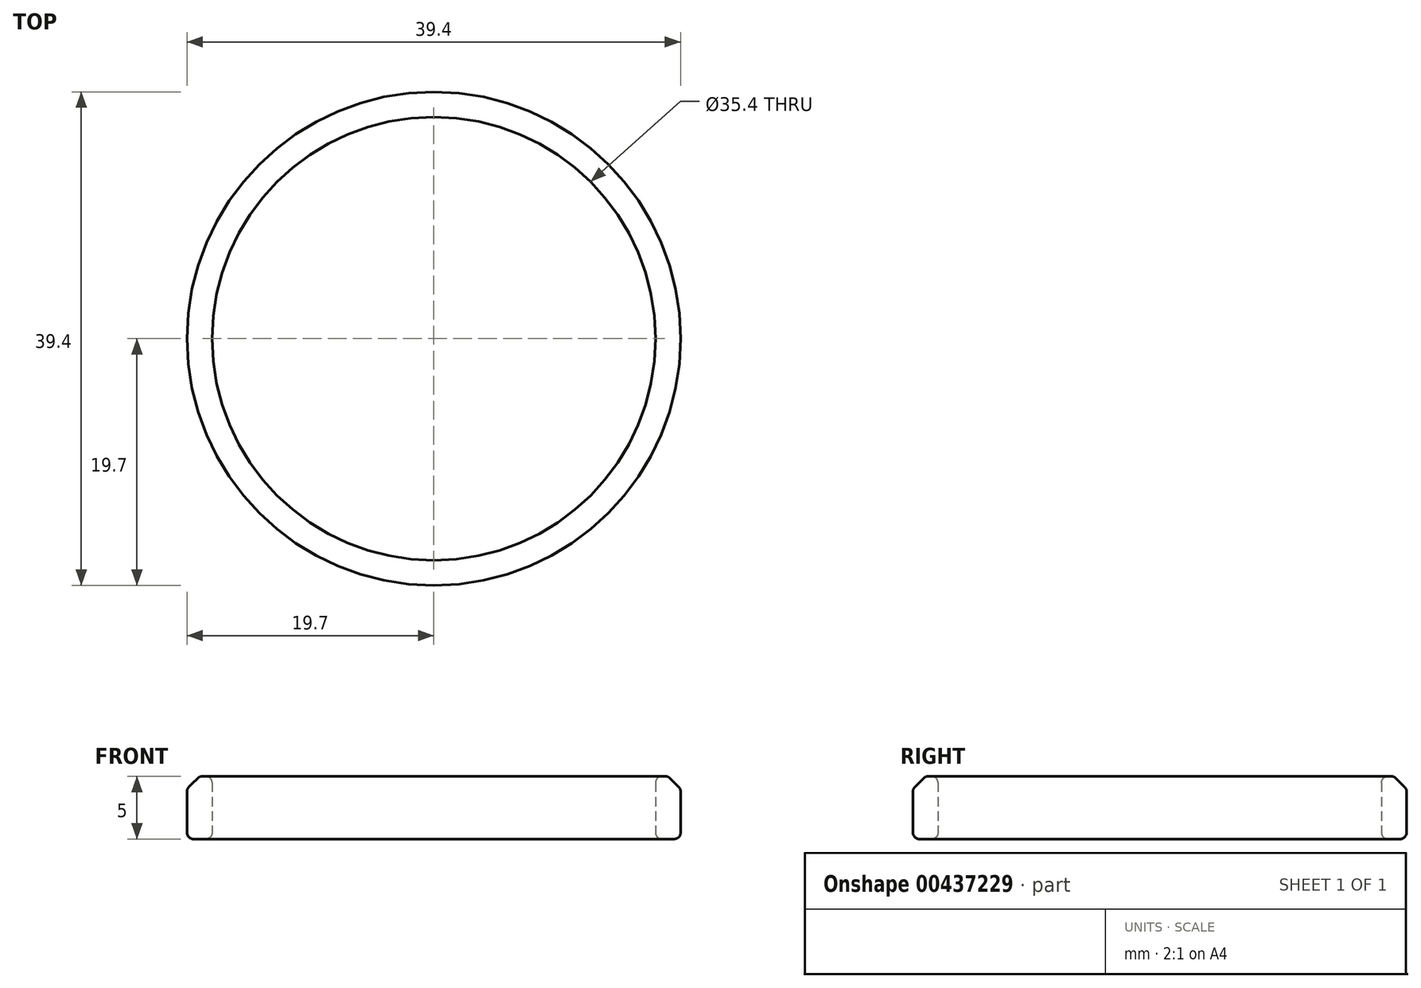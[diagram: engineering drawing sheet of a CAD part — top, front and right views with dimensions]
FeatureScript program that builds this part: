
annotation { "Feature Type Name" : "Feature", "Feature Type Description" : "" }
export const myFeature = defineFeature(function(context is Context, id is Id, definition is map)
    precondition{}
    {
        {
            var Q0;
            Q0=qCreatedBy(makeId("Top.planeOp"),FACE);
            var sketch = newSketch(context, id + "F0", { "sketchPlane" : qUnion([Q0])});
            skCircle(sketch, "E0", {"center": v(0, 0) * mm, "radius": 19.7 * mm});
            skSolve(sketch);
        }
        {
            var Q0;
            Q0=makeQuery(id+"F0.imprint","IMPRINT",FACE,{"disambiguationData":[TD([[makeQuery(id+"F0.imprint","IMPRINT",EDGE,{"derivedFrom":sQuery(id+"F0.wireOp",EDGE,"E0")}),1.0]])]});
            extrude(context, id + "F1", {"entities" : qUnion([Q0]), "depth" : 5 * mm});
        }
        {
            var Q0;
            Q0=makeQuery(id+"F1.opExtrude","CAP_FACE",FACE,{"disambiguationData":[OSD([sQuery(id+"F0.wireOp",EDGE,"E0")])],"isStart":false});
            var Q1;
            Q1=makeQuery(id+"F1.opExtrude","CAP_FACE",FACE,{"disambiguationData":[OSD([sQuery(id+"F0.wireOp",EDGE,"E0")])],"isStart":true});
            shell(context, id + "F2", {"entities" : qUnion([Q0, Q1]), "thickness" : 2 * mm});
        }
        {
            var Q0;
            Q0=makeQuery(id+"F1.opExtrude","CAP_EDGE",EDGE,{"disambiguationData":[OSD([sQuery(id+"F0.wireOp",EDGE,"E0")])],"isStart":false});
            chamfer(context, id + "F3", {"entities" : qUnion([Q0]), "width" : 1 * mm, "tangentPropagation" : true});
        }
        {
            var Q0;
            Q0=makeQuery(id+"F3.opChamfer","BLEND_FACE",FACE,{"disambiguationData":[OSD([sQuery(id+"F0.wireOp",EDGE,"E0")])]});
            var Q1;
            Q1=makeQuery(id+"F1.opExtrude","CAP_EDGE",EDGE,{"disambiguationData":[OSD([sQuery(id+"F0.wireOp",EDGE,"E0")])],"isStart":true});
            var Q2;
            {var subQ0=sQuery(id+"F0.wireOp",EDGE,"E0");Q2=makeQuery(id+"F2.opShell","OFFSET_EDGE",EDGE,{"disambiguationData":[OSD([subQ0]),TDD([makeQuery(id+"F1.opExtrude","CAP_EDGE",EDGE,{"disambiguationData":[OSD([subQ0])],"isStart":false})])]});}
            var Q3;
            {var subQ0=sQuery(id+"F0.wireOp",EDGE,"E0");Q3=makeQuery(id+"F2.opShell","OFFSET_EDGE",EDGE,{"disambiguationData":[OSD([subQ0]),TDD([makeQuery(id+"F1.opExtrude","CAP_EDGE",EDGE,{"disambiguationData":[OSD([subQ0])],"isStart":true})])]});}
            fillet(context, id + "F4", {"entities" : qUnion([Q0, Q1, Q2, Q3]), "radius" : 0.5 * mm, "tangentPropagation" : true, "allowEdgeOverflow" : false});
        }
    });
